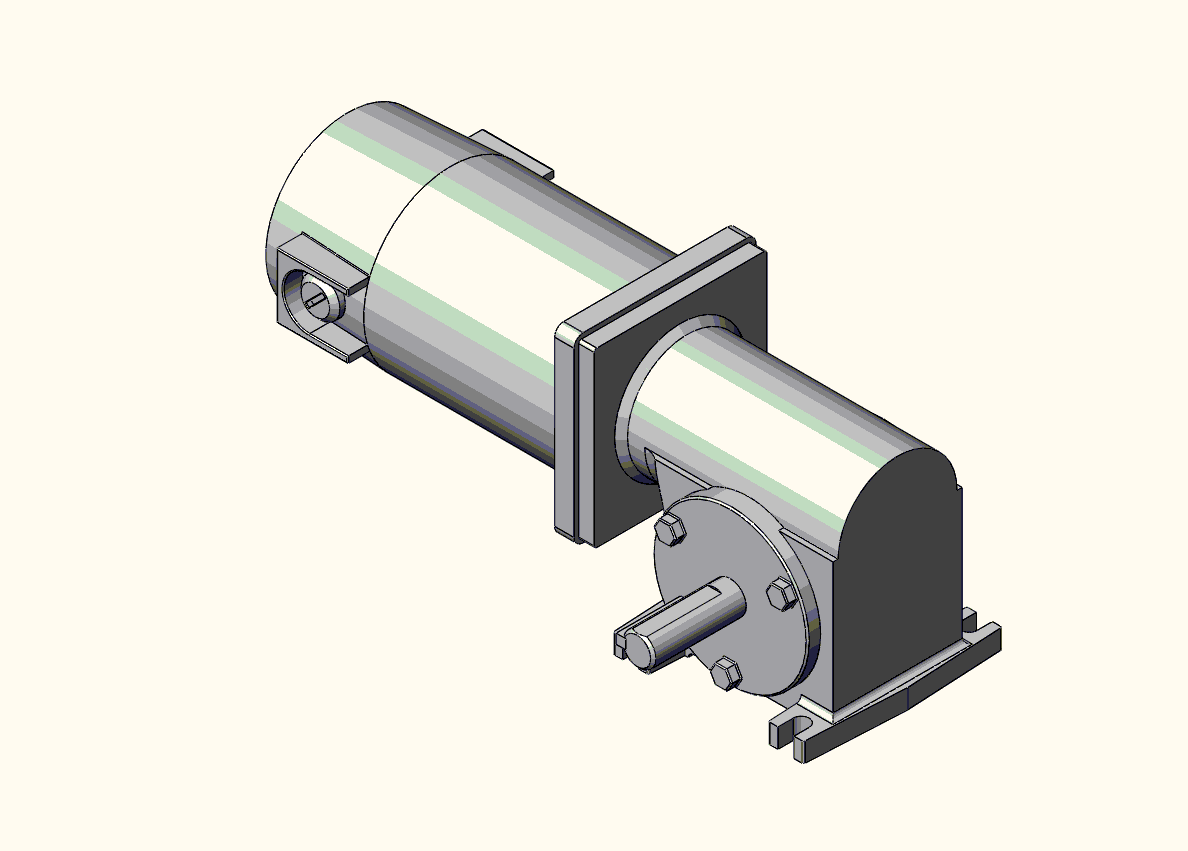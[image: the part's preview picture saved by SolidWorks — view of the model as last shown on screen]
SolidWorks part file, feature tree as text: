
SOLIDWORKS PART (.sldprt)
format: sldprt  version: not decoded by parser v0  size: 552,448 bytes
history: native  units: mm
features: sketch x17, extrude x11, fillet x7, chamfer x6, mirror x6, plane x5, cut_extrude x4, revolve x2, material x1, pattern_circular x1 (+14 scaffold rows collapsed)
feature tree (74):
  scaffold x14  (default folders/planes/origin — collapsed)
  material  "Material <not specified>"
  sketch  "Sketch1"  dims[c1.P=85.852mm c1.D1=44.45mm c1.XH=155.956mm c1.D2=6.35mm c1.D3=19.05mm c1.D4=0.508mm c2.D1=~90.256648mm c3.D1=3.0deg c3.D2=50.8mm]
  revolve  "Revolve1"  Angle=360deg
  plane  "Plane1"  Offset=83.82mm
  sketch  "Sketch3"  dims[c1.D1=~9.096518mm c1.D3=15.875mm c2.D1=59.69mm c2.D2=33.8582mm c3.D1=70.104mm]
  extrude  "Extrude1"  [1 undecoded]
  sketch  "Sketch4"  dims[c1.D1=15.0622mm c1.D2=10.8585mm c1.D3=4.8006mm c2.D2=4.8006mm]
  cut_extrude  "Cut-Extrude1"  Depth=38.1mm
  chamfer  "Chamfer6"  Distance=1.27mm Angle=45deg
  plane  "Plane2"  Offset=45.72mm
  sketch  "Sketch5"  dims[X=92.202mm]
  extrude  "Extrude2"  Depth=6.3754mm
  sketch  "Sketch6"  dims[c1.D3=65.024mm c1.D1=7.62mm c1.D2=58.42mm c2.D3=19.05mm c2.D4=~52.352646mm c3.D4=10.0deg c3.D3=114.3mm c4.D4=0.508mm]
  revolve  "Revolve6"  Angle=360deg
  plane  "Plane3"  Offset=76.2mm
  sketch  "Sketch7"
  extrude  "Extrude3"  [1 undecoded]
  fillet  "Fillet1"  Radius=12.7mm
  chamfer  "Chamfer2"  Distance=3.175mm Angle=45deg
  sketch  "Sketch15"  dims[D1=0.0mm]
  extrude  "Extrude7"  [1 undecoded]
  mirror  "Mirror1"
  sketch  "Sketch8"  dims[c1.D1=0.0254mm c1.D2=0.0254mm c1.D3=0.0254mm c2.D1=0.0254mm c2.D3=0.0254mm]
  extrude  "Extrude4"  Depth=31.75mm
  sketch  "Sketch9"  dims[D1=19.05mm D2=31.75mm]
  extrude  "Extrude5"  Depth=95.25mm PB=95.25mm
  chamfer  "Chamfer3"  Distance=2.54mm Angle=45deg
  sketch  "Sketch10"  dims[c1.D1=2.032mm c1.D2=11.43mm c1.D3=~5.30526mm c2.D3=45.0deg]
  cut_extrude  "Cut-Extrude2"  Depth=2.54mm
  mirror  "Mirror5"
  chamfer  "Chamfer4"  Distance=0.254mm Angle=45deg
  sketch  "Sketch16"  dims[D1=31.75mm D2=3.175mm D3=15.875mm]
  extrude  "Extrude8"  Depth=101.6mm
  fillet  "Fillet2"  Radius=0.508mm
  sketch  "Sketch13"  dims[c1.D1=~14.903383mm c2.D1=20.0deg c2.D2=9.525mm c2.D3=31.75mm]
  extrude  "Extrude6"  Depth=4.7498mm
  chamfer  "Chamfer5"  Distance=0.508mm Angle=45deg
  pattern_circular  "CirPattern2"  Count=3 Angle=360deg
  mirror  "Mirror6"
  plane  "Plane4"  Offset=15.113mm
  chamfer  "Chamfer7"  Distance=0.762mm Angle=45deg
  sketch  "Sketch17"  dims[c1.D1=50.8mm c1.D2=2.54mm c2.D1=26.924mm]
  cut_extrude  "Cut-Extrude3"  [1 undecoded]
  fillet  "Fillet3"  Radius=2.54mm
  sketch  "Sketch18"  dims[c1.D1=49.276mm c1.D2=38.1mm c1.D3=~79.904069mm c2.D3=92.0deg c3.D3=97.536mm c3.D1=98.552mm c3.D4=~49.393976mm c4.D4=93.0deg]
  extrude  "Extrude9"  Depth=9.525mm
  plane  "Plane5"
  mirror  "Mirror7"
  sketch  "Sketch19"  dims[c1.D2=3.937mm c1.D1=7.874mm c2.D2=82.55mm]
  cut_extrude  "Cut-Extrude4"  [1 undecoded]
  mirror  "Mirror8"
  mirror  "Mirror9"
  fillet  "Fillet4"  Radius=0.762mm
  fillet  "Fillet5"  Radius=2.54mm
  sketch  "Sketch20"  dims[D1=120.904mm]
  extrude  "Extrude10"  Depth=9.525mm
  fillet  "Fillet6"  Radius=4.445mm
  sketch  "Sketch21"
  extrude  "Extrude11"  [1 undecoded]
  fillet  "Fillet7"  Radius=1.27mm hex flats=14.2748mm hex flats/2=7.366mm
decode coverage: 40 of 54 modeling features carry decoded parameters
note: ~ marks probable driven/reference dimensions
note: 6 parameter values undecoded
summary: no parameter record found for 6 features
note: suppression state not decoded; provenance and decode notes live in map.json
